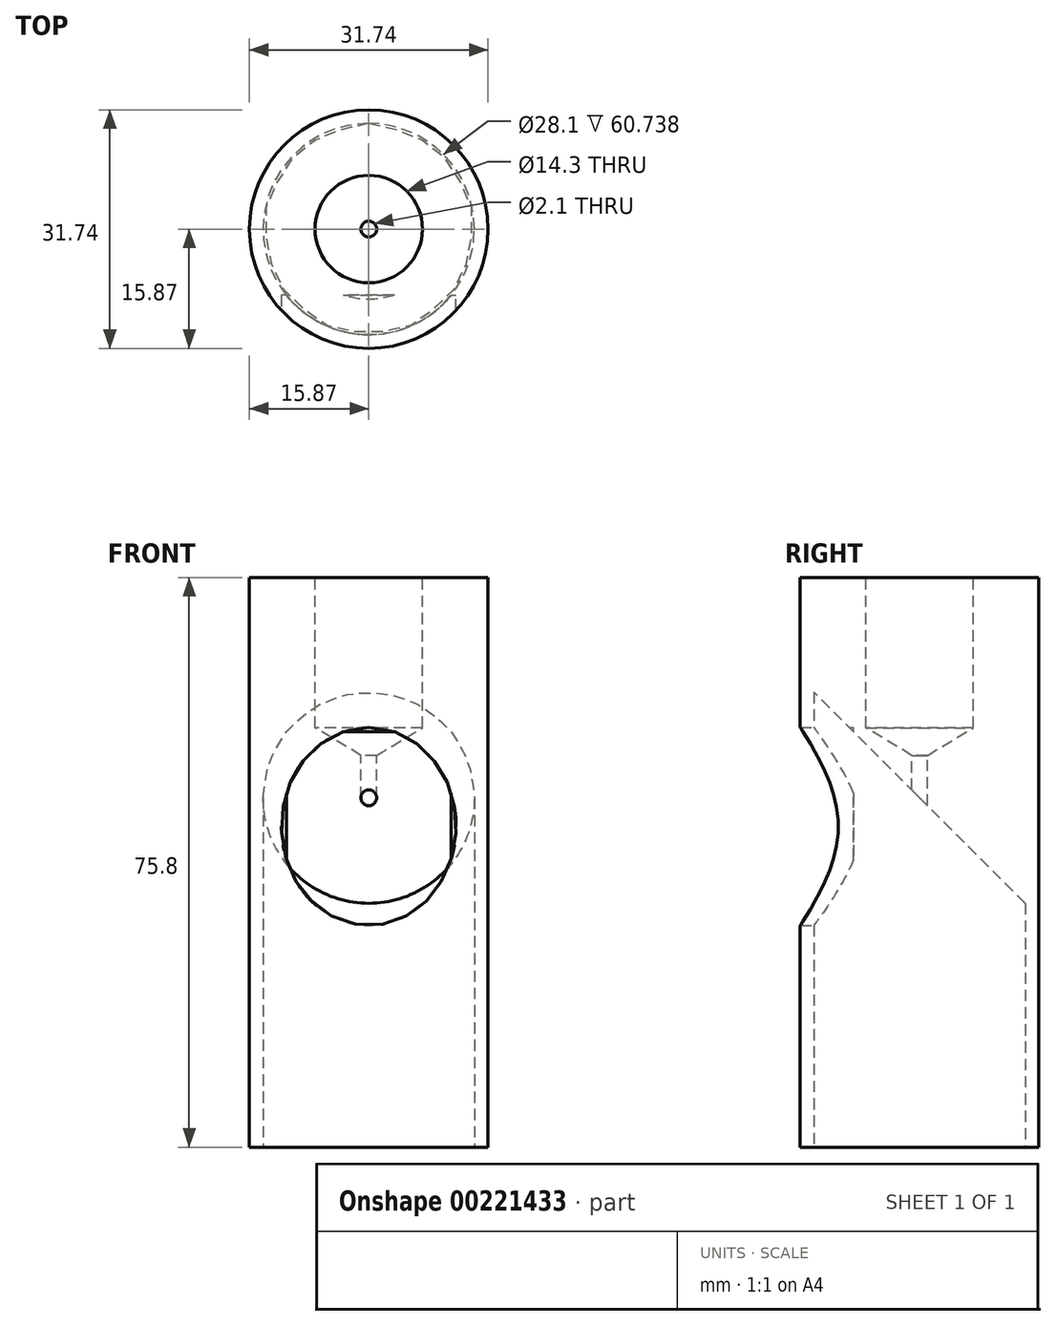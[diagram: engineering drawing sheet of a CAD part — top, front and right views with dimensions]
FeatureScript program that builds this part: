
annotation { "Feature Type Name" : "Feature", "Feature Type Description" : "" }
export const myFeature = defineFeature(function(context is Context, id is Id, definition is map)
    precondition{}
    {
        {
            var Q0;
            Q0=qCreatedBy(makeId("Top.planeOp"),FACE);
            var sketch = newSketch(context, id + "F0", { "sketchPlane" : qUnion([Q0])});
            skCircle(sketch, "E0", {"center": v(0, 0) * mm, "radius": 15.87 * mm});
            skSolve(sketch);
        }
        {
            var Q0;
            Q0=makeQuery(id+"F0.imprint","IMPRINT",FACE,{"disambiguationData":[TD([[makeQuery(id+"F0.imprint","IMPRINT",EDGE,{"derivedFrom":sQuery(id+"F0.wireOp",EDGE,"E0")}),1.0]])]});
            extrude(context, id + "F1", {"entities" : qUnion([Q0]), "depth" : 50.8 * mm});
        }
        {
            var Q0;
            Q0=makeQuery(id+"F1.opExtrude","CAP_FACE",FACE,{"disambiguationData":[OSD([sQuery(id+"F0.wireOp",EDGE,"E0")])],"isStart":false});
            var sketch = newSketch(context, id + "F2", { "sketchPlane" : qUnion([Q0])});
            skPoint(sketch, "E1", {"position": v(0, 0) * mm});
            skCircle(sketch, "E2", {"center": v(0, 0) * mm, "radius": 1.05 * mm});
            skSolve(sketch);
        }
        {
            var Q0;
            Q0=qCreatedBy(makeId("Right.planeOp"),FACE);
            var sketch = newSketch(context, id + "F3", { "sketchPlane" : qUnion([Q0])});
            skLineSegment(sketch, "E3", {"start": v(21.5, 0) * mm, "end": v(-31.65, 53.15) * mm});
            skSolve(sketch);
        }
        {
            var Q0;
            Q0=sQuery(id+"F3.wireOp",EDGE,"E3");
            extrude(context, id + "F4", {"bodyType" : ToolBodyType.SURFACE, "surfaceEntities" : qUnion([Q0]), "depth" : 37.6 * mm, "hasSecondDirection" : true, "secondDirectionOppositeDirection" : true, "secondDirectionDepth" : 25 * mm});
        }
        {
            var Q0;
            Q0=qCreatedBy(makeId("Top.planeOp"),FACE);
            var sketch = newSketch(context, id + "F5", { "sketchPlane" : qUnion([Q0])});
            skCircle(sketch, "E4", {"center": v(0, 0) * mm, "radius": 14.05 * mm});
            skSolve(sketch);
        }
        {
            var Q0;
            Q0 = qSketchRegion(id + "F5", true);
            var Q1;
            Q1=makeQuery(id+"F4.opExtrude","SWEPT_FACE",FACE,{"disambiguationData":[OSD([sQuery(id+"F3.wireOp",EDGE,"E3")])]});
            extrude(context, id + "F6", {"entities" : qUnion([Q0]), "operationType" : NewBodyOperationType.REMOVE, "endBound" : BoundingType.UP_TO_SURFACE, "endBoundEntityFace" : qUnion([Q1]), "depth" : 25 * mm});
        }
        {
            var Q0;
            Q0=sQuery(id+"F2.wireOp",VERTEX,"E1");
            var Q1;
            Q1=makeQuery(id+"F1.opExtrude","SWEPT_BODY",BODY,{"disambiguationData":[OSD([sQuery(id+"F0.wireOp",EDGE,"E0")])]});
            hole(context, id + "F7", {"style" : HoleStyle.SIMPLE, "endStyle" : HoleEndStyle.BLIND, "holeDiameter" : 14.3 * mm, "holeDepth" : 20 * mm, "locations" : qUnion([Q0]), "scope" : qUnion([Q1])});
        }
        {
            var Q0;
            Q0 = qSketchRegion(id + "F2", true);
            extrude(context, id + "F8", {"entities" : qUnion([Q0]), "operationType" : NewBodyOperationType.REMOVE, "oppositeDirection" : true, "depth" : 86.1 * mm});
        }
        {
            var Q0;
            Q0=qCreatedBy(makeId("Front.planeOp"),FACE);
            cPlane(context, id + "F9", {"entities" : qUnion([Q0]), "cplaneType" : CPlaneType.OFFSET, "offset" : 8.8 * mm, "width" : 150 * mm, "height" : 150 * mm});
        }
        {
            var Q0;
            Q0=qCreatedBy(id+"F9.planeOp",FACE);
            var sketch = newSketch(context, id + "F10", { "sketchPlane" : qUnion([Q0])});
            skEllipse(sketch, "E5", {"center": v(0, 17.7) * mm, "majorRadius": 13.18 * mm, "minorRadius": 11.62 * mm, "majorAxis": v(0, 1)});
            skSolve(sketch);
        }
        {
            var Q0;
            Q0 = qSketchRegion(id + "F10", true);
            extrude(context, id + "F11", {"entities" : qUnion([Q0]), "operationType" : NewBodyOperationType.REMOVE, "depth" : 25 * mm});
        }
        {
            var Q0;
            Q0=makeQuery(id+"F1.opExtrude","CAP_FACE",FACE,{"disambiguationData":[OSD([sQuery(id+"F0.wireOp",EDGE,"E0")])],"isStart":true});
            extrude(context, id + "F12", {"entities" : qUnion([Q0]), "operationType" : NewBodyOperationType.ADD, "depth" : 25 * mm});
        }
        {
            var Q0;
            Q0=makeQuery(id+"F4.opExtrude","SWEPT_BODY",BODY,{"disambiguationData":[OSD([sQuery(id+"F3.wireOp",EDGE,"E3")])]});
            deleteBodies(context, id + "F13", {"entities" : qUnion([Q0])});
        }
    });
